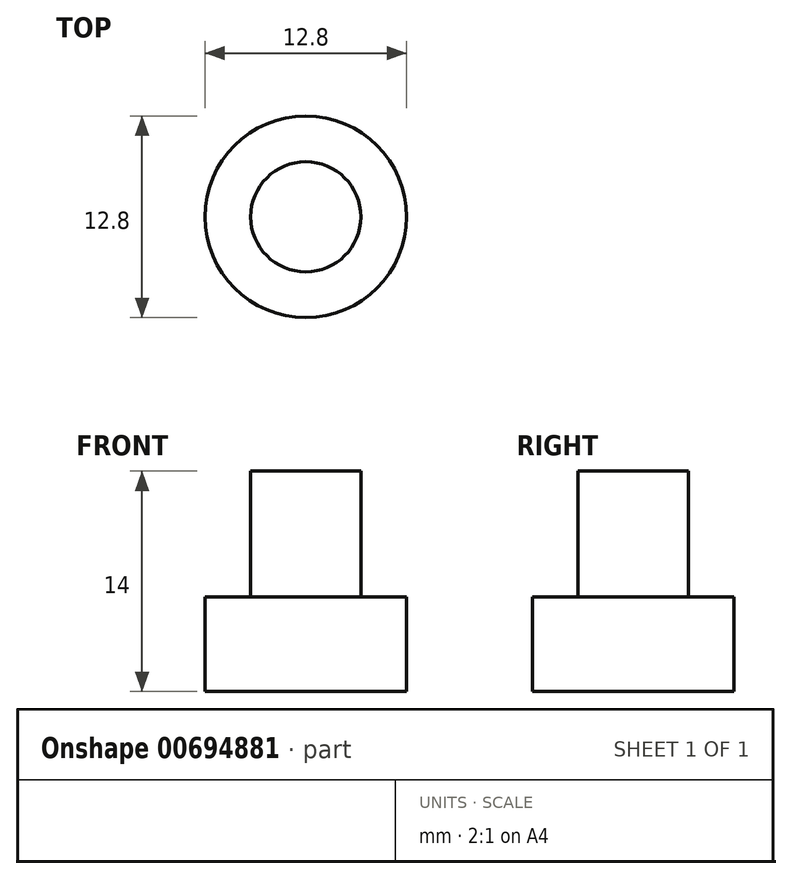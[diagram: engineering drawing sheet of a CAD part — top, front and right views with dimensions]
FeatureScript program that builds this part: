
annotation { "Feature Type Name" : "Feature", "Feature Type Description" : "" }
export const myFeature = defineFeature(function(context is Context, id is Id, definition is map)
    precondition{}
    {
        {
            var Q0;
            Q0=qCreatedBy(makeId("Top.planeOp"),FACE);
            var sketch = newSketch(context, id + "F0", { "sketchPlane" : qUnion([Q0])});
            skCircle(sketch, "E0", {"center": v(0, 0) * mm, "radius": 6.4 * mm});
            skCircle(sketch, "E1", {"center": v(0, 0) * mm, "radius": 3.5 * mm});
            skSolve(sketch);
        }
        {
            var Q0;
            Q0=makeQuery(id+"F0.imprint","IMPRINT",FACE,{"disambiguationData":[TD([[makeQuery(id+"F0.imprint","IMPRINT",EDGE,{"derivedFrom":sQuery(id+"F0.wireOp",EDGE,"E1")}),1.0]])]});
            extrude(context, id + "F1", {"entities" : qUnion([Q0]), "depth" : 8 * mm, "offsetDistance" : 25 * mm});
        }
        {
            var Q0;
            Q0=makeQuery(id+"F0.imprint","IMPRINT",FACE,{"disambiguationData":[TD([[makeQuery(id+"F0.imprint","IMPRINT",EDGE,{"derivedFrom":sQuery(id+"F0.wireOp",EDGE,"E0")}),1.0]])]});
            var Q1;
            Q1=makeQuery(id+"F0.imprint","IMPRINT",FACE,{"disambiguationData":[TD([[makeQuery(id+"F0.imprint","IMPRINT",EDGE,{"derivedFrom":sQuery(id+"F0.wireOp",EDGE,"E1")}),1.0]])]});
            extrude(context, id + "F2", {"entities" : qUnion([Q0, Q1]), "operationType" : NewBodyOperationType.ADD, "depth" : -6 * mm, "offsetDistance" : 25 * mm});
        }
    });
